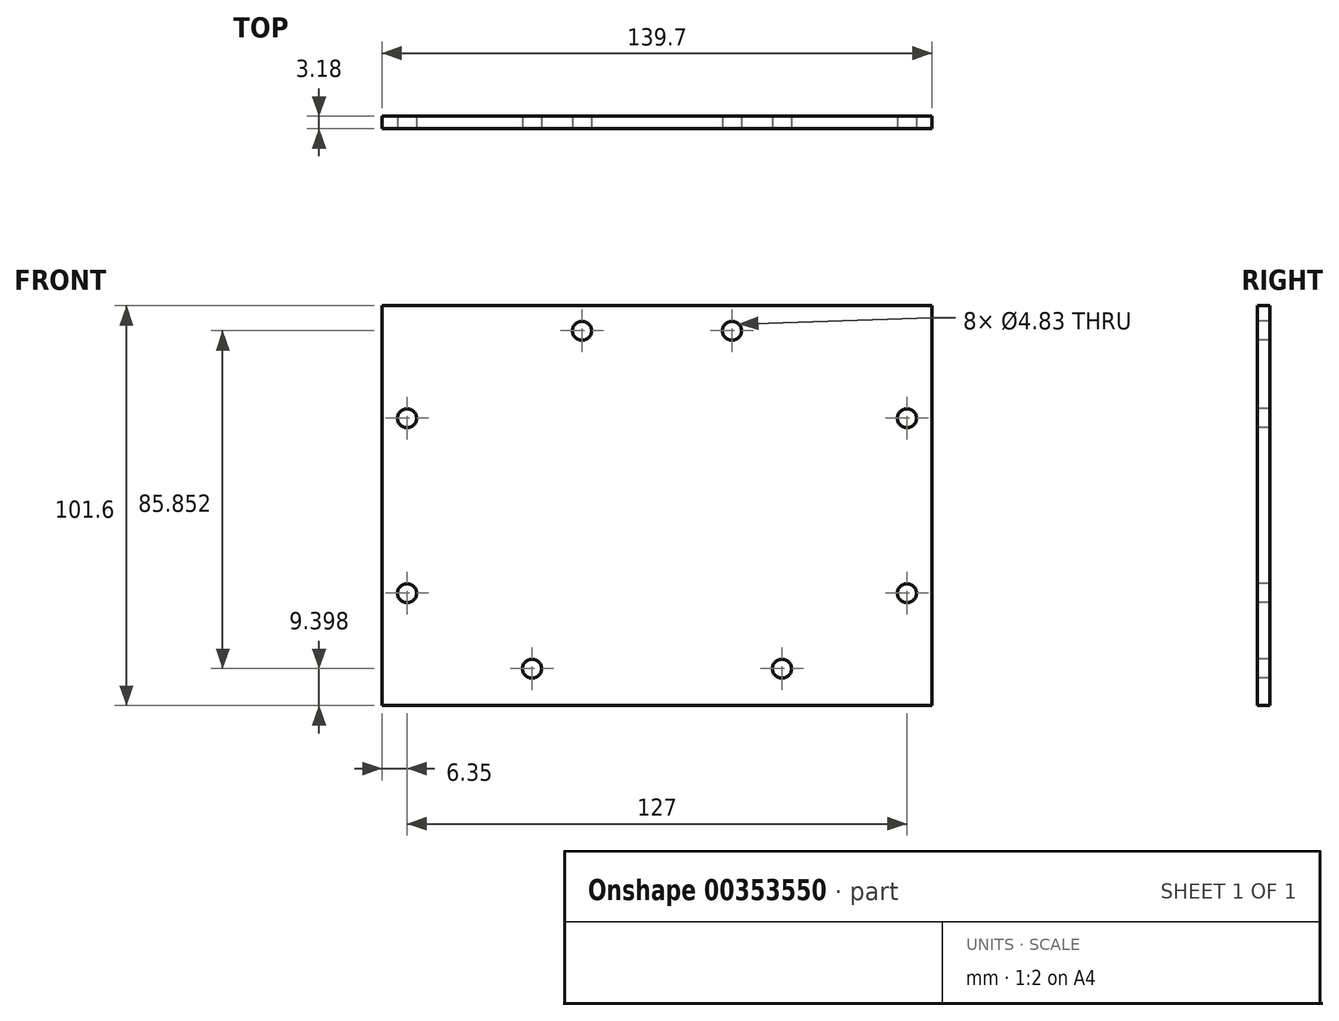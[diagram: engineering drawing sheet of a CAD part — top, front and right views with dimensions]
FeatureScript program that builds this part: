
annotation { "Feature Type Name" : "Feature", "Feature Type Description" : "" }
export const myFeature = defineFeature(function(context is Context, id is Id, definition is map)
    precondition{}
    {
        {
            var Q0;
            Q0=qCreatedBy(makeId("Front.planeOp"),FACE);
            var sketch = newSketch(context, id + "F0", { "sketchPlane" : qUnion([Q0])});
            skLineSegment(sketch, "E0.bottom", {"start": v(-69.85, 50.8) * mm, "end": v(69.85, 50.8) * mm});
            skLineSegment(sketch, "E0.top", {"start": v(-69.85, -50.8) * mm, "end": v(69.85, -50.8) * mm});
            skLineSegment(sketch, "E0.left", {"start": v(-69.85, 50.8) * mm, "end": v(-69.85, -50.8) * mm});
            skLineSegment(sketch, "E0.right", {"start": v(69.85, 50.8) * mm, "end": v(69.85, -50.8) * mm});
            skPoint(sketch, "E0.middle", {"position": v(0, 0) * mm});
            skSolve(sketch);
        }
        {
            var Q0;
            Q0 = qSketchRegion(id + "F0", true);
            extrude(context, id + "F1", {"entities" : qUnion([Q0]), "depth" : 3.17 * mm});
        }
        {
            var Q0;
            Q0=makeQuery(id+"F1.opExtrude","CAP_FACE",FACE,{"disambiguationData":[OSD([sQuery(id+"F0.wireOp",EDGE,"E0.bottom"),sQuery(id+"F0.wireOp",EDGE,"E0.top"),sQuery(id+"F0.wireOp",EDGE,"E0.left"),sQuery(id+"F0.wireOp",EDGE,"E0.right")])],"isStart":false});
            var sketch = newSketch(context, id + "F2", { "sketchPlane" : qUnion([Q0])});
            skCircle(sketch, "E1", {"center": v(-19.05, 44.45) * mm, "radius": 2.41 * mm});
            skSolve(sketch);
        }
        {
            var Q0;
            Q0 = qSketchRegion(id + "F2", true);
            extrude(context, id + "F3", {"entities" : qUnion([Q0]), "operationType" : NewBodyOperationType.REMOVE, "endBound" : BoundingType.THROUGH_ALL, "oppositeDirection" : true, "depth" : 25.4 * mm});
        }
        {
            var Q0;
            Q0=makeQuery(id+"F1.opExtrude","CAP_FACE",FACE,{"disambiguationData":[OSD([sQuery(id+"F0.wireOp",EDGE,"E0.bottom"),sQuery(id+"F0.wireOp",EDGE,"E0.top"),sQuery(id+"F0.wireOp",EDGE,"E0.left"),sQuery(id+"F0.wireOp",EDGE,"E0.right")])],"isStart":false});
            var sketch = newSketch(context, id + "F4", { "sketchPlane" : qUnion([Q0])});
            skCircle(sketch, "E2", {"center": v(19.05, 44.45) * mm, "radius": 2.41 * mm});
            skSolve(sketch);
        }
        {
            var Q0;
            Q0 = qSketchRegion(id + "F4", true);
            extrude(context, id + "F5", {"entities" : qUnion([Q0]), "operationType" : NewBodyOperationType.REMOVE, "endBound" : BoundingType.THROUGH_ALL, "oppositeDirection" : true, "depth" : 25.4 * mm});
        }
        {
            var Q0;
            Q0=makeQuery(id+"F1.opExtrude","CAP_FACE",FACE,{"disambiguationData":[OSD([sQuery(id+"F0.wireOp",EDGE,"E0.bottom"),sQuery(id+"F0.wireOp",EDGE,"E0.top"),sQuery(id+"F0.wireOp",EDGE,"E0.left"),sQuery(id+"F0.wireOp",EDGE,"E0.right")])],"isStart":false});
            var sketch = newSketch(context, id + "F6", { "sketchPlane" : qUnion([Q0])});
            skCircle(sketch, "E3", {"center": v(-31.75, -41.4) * mm, "radius": 2.41 * mm});
            skSolve(sketch);
        }
        {
            var Q0;
            Q0 = qSketchRegion(id + "F6", true);
            extrude(context, id + "F7", {"entities" : qUnion([Q0]), "operationType" : NewBodyOperationType.REMOVE, "endBound" : BoundingType.THROUGH_ALL, "oppositeDirection" : true, "depth" : 25.4 * mm});
        }
        {
            var Q0;
            Q0=makeQuery(id+"F1.opExtrude","CAP_FACE",FACE,{"disambiguationData":[OSD([sQuery(id+"F0.wireOp",EDGE,"E0.bottom"),sQuery(id+"F0.wireOp",EDGE,"E0.top"),sQuery(id+"F0.wireOp",EDGE,"E0.left"),sQuery(id+"F0.wireOp",EDGE,"E0.right")])],"isStart":false});
            var sketch = newSketch(context, id + "F8", { "sketchPlane" : qUnion([Q0])});
            skCircle(sketch, "E4", {"center": v(31.75, -41.4) * mm, "radius": 2.41 * mm});
            skCircle(sketch, "E5.0", {"center": v(-31.75, -41.4) * mm, "radius": 2.41 * mm});
            skSolve(sketch);
        }
        {
            var Q0;
            Q0 = qSketchRegion(id + "F8", true);
            extrude(context, id + "F9", {"entities" : qUnion([Q0]), "operationType" : NewBodyOperationType.REMOVE, "endBound" : BoundingType.THROUGH_ALL, "oppositeDirection" : true, "depth" : 25.4 * mm});
        }
        {
            var Q0;
            Q0=makeQuery(id+"F1.opExtrude","CAP_FACE",FACE,{"disambiguationData":[OSD([sQuery(id+"F0.wireOp",EDGE,"E0.bottom"),sQuery(id+"F0.wireOp",EDGE,"E0.top"),sQuery(id+"F0.wireOp",EDGE,"E0.left"),sQuery(id+"F0.wireOp",EDGE,"E0.right")])],"isStart":false});
            var sketch = newSketch(context, id + "F10", { "sketchPlane" : qUnion([Q0])});
            skCircle(sketch, "E6", {"center": v(-63.5, 22.23) * mm, "radius": 2.41 * mm});
            skSolve(sketch);
        }
        {
            var Q0;
            Q0 = qSketchRegion(id + "F10", true);
            extrude(context, id + "F11", {"entities" : qUnion([Q0]), "operationType" : NewBodyOperationType.REMOVE, "endBound" : BoundingType.THROUGH_ALL, "oppositeDirection" : true, "depth" : 25.4 * mm});
        }
        {
            var Q0;
            Q0=makeQuery(id+"F1.opExtrude","CAP_FACE",FACE,{"disambiguationData":[OSD([sQuery(id+"F0.wireOp",EDGE,"E0.bottom"),sQuery(id+"F0.wireOp",EDGE,"E0.top"),sQuery(id+"F0.wireOp",EDGE,"E0.left"),sQuery(id+"F0.wireOp",EDGE,"E0.right")])],"isStart":false});
            var sketch = newSketch(context, id + "F12", { "sketchPlane" : qUnion([Q0])});
            skCircle(sketch, "E7", {"center": v(-63.5, -22.23) * mm, "radius": 2.41 * mm});
            skSolve(sketch);
        }
        {
            var Q0;
            Q0 = qSketchRegion(id + "F12", true);
            extrude(context, id + "F13", {"entities" : qUnion([Q0]), "operationType" : NewBodyOperationType.REMOVE, "endBound" : BoundingType.THROUGH_ALL, "oppositeDirection" : true, "depth" : 25.4 * mm});
        }
        {
            var Q0;
            Q0=makeQuery(id+"F1.opExtrude","CAP_FACE",FACE,{"disambiguationData":[OSD([sQuery(id+"F0.wireOp",EDGE,"E0.bottom"),sQuery(id+"F0.wireOp",EDGE,"E0.top"),sQuery(id+"F0.wireOp",EDGE,"E0.left"),sQuery(id+"F0.wireOp",EDGE,"E0.right")])],"isStart":false});
            var sketch = newSketch(context, id + "F14", { "sketchPlane" : qUnion([Q0])});
            skCircle(sketch, "E8", {"center": v(63.5, 22.23) * mm, "radius": 2.41 * mm});
            skSolve(sketch);
        }
        {
            var Q0;
            Q0 = qSketchRegion(id + "F14", true);
            extrude(context, id + "F15", {"entities" : qUnion([Q0]), "operationType" : NewBodyOperationType.REMOVE, "endBound" : BoundingType.THROUGH_ALL, "oppositeDirection" : true, "depth" : 25.4 * mm});
        }
        {
            var Q0;
            Q0=makeQuery(id+"F1.opExtrude","CAP_FACE",FACE,{"disambiguationData":[OSD([sQuery(id+"F0.wireOp",EDGE,"E0.bottom"),sQuery(id+"F0.wireOp",EDGE,"E0.top"),sQuery(id+"F0.wireOp",EDGE,"E0.left"),sQuery(id+"F0.wireOp",EDGE,"E0.right")])],"isStart":false});
            var sketch = newSketch(context, id + "F16", { "sketchPlane" : qUnion([Q0])});
            skCircle(sketch, "E9", {"center": v(63.5, -22.23) * mm, "radius": 2.41 * mm});
            skCircle(sketch, "E10.0", {"center": v(63.5, 22.23) * mm, "radius": 2.41 * mm});
            skSolve(sketch);
        }
        {
            var Q0;
            Q0 = qSketchRegion(id + "F16", true);
            extrude(context, id + "F17", {"entities" : qUnion([Q0]), "operationType" : NewBodyOperationType.REMOVE, "endBound" : BoundingType.THROUGH_ALL, "oppositeDirection" : true, "depth" : 25.4 * mm});
        }
    });
